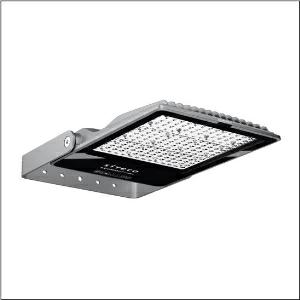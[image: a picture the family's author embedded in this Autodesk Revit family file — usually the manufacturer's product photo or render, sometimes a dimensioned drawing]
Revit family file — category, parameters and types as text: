
# Revit family: sicompact_31_midi___pl32_5xa7581d2k23_8b39
name_source: partatom
category: Lighting Fixtures
units: mm (PartAtom-declared; Revit-internal decimal feet)

## family parameters
Cut with Voids When Loaded = No
Host = Face
Light Source = No
Part Type = Normal
Room Calculation Point = No
Round Connector Dimension = Use Diameter
Shared = No

## types (1)
- SiCompact 31 midi  PL32 (1 x LED, 27000 lm, 165 W, 4000K)
    Apparent Load = 165 VA
    CIE Flux Codes = 32 69 98 100 100
    Color Rendering = 70
    Color Temperature = 4000K
    Default Elevation = 1800 mm
    Description = SiCompact 31 midi, floodlight, primary light control with lens, of plastic, of toughened safety glass, transparent, light distribution: PL32, light emission: direct distribution, primary light characteristic: asymmetric, installation type: surface-mounted, LED, High Power LED, rated luminous flux: 27.000lm, luminous efficacy: 164lm/W, light colour: 740, colour temperature: 4000K, control gear: ON/OFF, with cable, 3x 1.5mm², mains connection: 220..240V, AC, 50/60Hz, connection cable pre-assembled, cable length: 2m, rated input power: 165W, of diecast aluminium, specular, metallic grey (RAL 9006), length: 560mm, width: 330mm, height: 62mm, bracket, of sheet steel, coated, metallic grey (RAL 9006), ON/OFF, protection rating (complete): IP66, insulation class (complete): insulation class I (protective earthing), certification: CE, ENEC, impact resistance: IK08, permissible operating ambient temperature: -40..+45°C, packaging unit: 1 piece

Light Distribution: PL32
    Height = 62 mm
    Lamp = 1 x LED
    Lamp Light Flux = 27000 lm
    Lamp Power = 165 W
    Lamp count = 1
    Length = 560 mm
    Luminous efficacy = 164 lm/W
    Manufacturer = Siteco
    ModVariant = No
    Model = 5XA7581D2K23
    Mounting Place = Wall
    Mounting Type = Surface mounted
    Number of Poles = 1
    OnlyDefault = Yes
    Power Factor = 1
    Product Name = SiCompact 31 midi | PL32
    Product group = floodlight | wall mounted
    ProductGroupID = 2002
    Protection Class = Protection class I
    Protection Degree = IP 66
    RLX_Detail_Level = 1
    RLX_Emergency_Light_Flux = 0 lm
    RLX_Emergency_Type = 0
    RLX_Emergency_Type_DB = No
    RlxData = <blob elided: 98201 chars, md5=dafcc1c1>
    Socket = socket
    Standby Power = 0 W
    System Light Flux = 27000 lm
    System Power = 165 W
    Type Comments = Product without accessories
    Type Image = l_1006415.jpg
    URL = http://relux.com
    VarID = ---
    Voltage = 0 V
    Weight = 0.00 kg
    Width = 333 mm

## geometry (parser evidence)
native form markers: Blend x4, Sweep x10
no freeform markers — native parametric forms only
